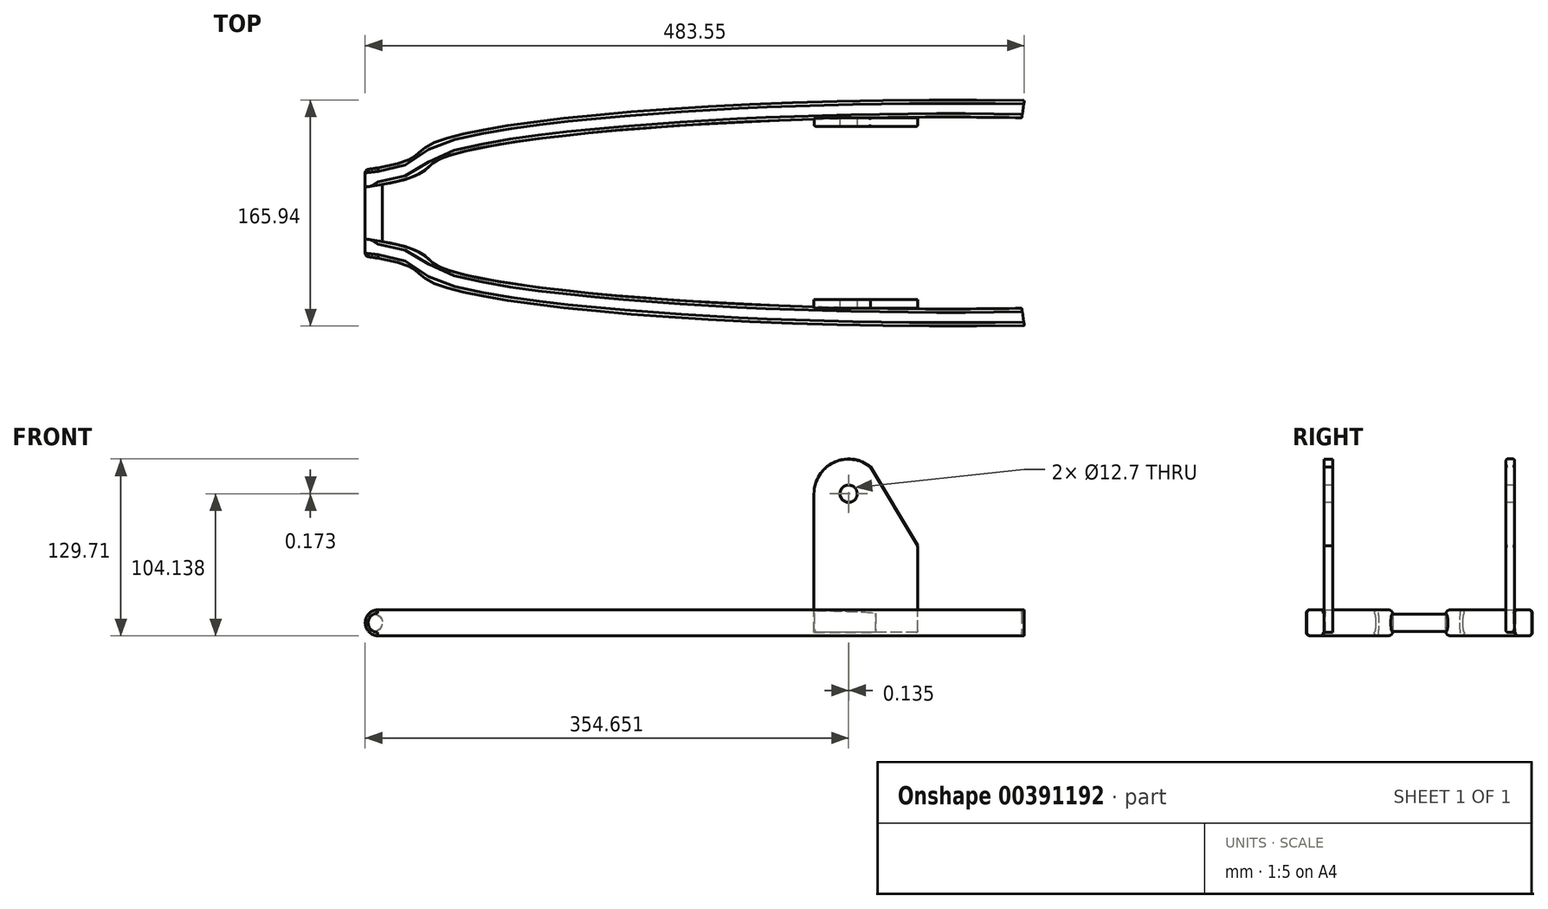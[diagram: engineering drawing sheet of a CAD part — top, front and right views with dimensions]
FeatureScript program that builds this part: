
annotation { "Feature Type Name" : "Feature", "Feature Type Description" : "" }
export const myFeature = defineFeature(function(context is Context, id is Id, definition is map)
    precondition{}
    {
        {
            var Q0;
            Q0=qCreatedBy(makeId("Front.planeOp"),FACE);
            var sketch = newSketch(context, id + "F0", { "sketchPlane" : qUnion([Q0])});
            skCircle(sketch, "E0", {"center": v(-33.3, 34.5) * mm, "radius": 6.35 * mm});
            skLineSegment(sketch, "E1", {"start": v(-33.3, 34.5) * mm, "end": v(-26.96, 34.5) * mm, "construction": true});
            skLineSegment(sketch, "E2", {"start": v(-33.3, 34.5) * mm, "end": v(-39.66, 34.5) * mm, "construction": true});
            skSolve(sketch);
        }
        {
            var Q0;
            Q0=makeQuery(id+"F0.imprint","IMPRINT",FACE,{"disambiguationData":[TD([[makeQuery(id+"F0.imprint","IMPRINT",EDGE,{"derivedFrom":sQuery(id+"F0.wireOp",EDGE,"E0")}),1.0]])]});
            var Q1;
            Q1 = qSketchRegion(id + "F0", true);
            extrude(context, id + "F1", {"entities" : qUnion([Q0, Q1]), "depth" : 50.8 * mm});
        }
        {
            var Q0;
            Q0=sQuery(id+"F0.wireOp",VERTEX,"E2.end");
            var Q1;
            Q1=qCreatedBy(makeId("Right.planeOp"),FACE);
            cPlane(context, id + "F2", {"entities" : qUnion([Q0, Q1]), "cplaneType" : CPlaneType.PLANE_POINT, "offset" : 25.4 * mm, "width" : 152.4 * mm, "height" : 152.4 * mm});
        }
        {
            var Q0;
            Q0=qCreatedBy(id+"F2.planeOp",FACE);
            var sketch = newSketch(context, id + "F3", { "sketchPlane" : qUnion([Q0])});
            skLineSegment(sketch, "E3.bottom", {"start": v(6.35, 44.02) * mm, "end": v(-6.35, 44.02) * mm});
            skLineSegment(sketch, "E3.top", {"start": v(6.35, 24.97) * mm, "end": v(-6.35, 24.97) * mm});
            skLineSegment(sketch, "E3.left", {"start": v(6.35, 44.02) * mm, "end": v(6.35, 24.97) * mm});
            skLineSegment(sketch, "E3.right", {"start": v(-6.35, 44.02) * mm, "end": v(-6.35, 24.97) * mm});
            skPoint(sketch, "E3.middle", {"position": v(0, 34.5) * mm});
            skLineSegment(sketch, "E4.bottom", {"start": v(-57.15, 44.02) * mm, "end": v(-44.45, 44.02) * mm});
            skLineSegment(sketch, "E4.top", {"start": v(-57.15, 24.97) * mm, "end": v(-44.45, 24.97) * mm});
            skLineSegment(sketch, "E4.left", {"start": v(-57.15, 44.02) * mm, "end": v(-57.15, 24.97) * mm});
            skLineSegment(sketch, "E4.right", {"start": v(-44.45, 44.02) * mm, "end": v(-44.45, 24.97) * mm});
            skPoint(sketch, "E4.middle", {"position": v(-50.8, 34.5) * mm});
            skSolve(sketch);
        }
        {
            var Q0;
            Q0=sQuery(id+"F3.wireOp",VERTEX,"E3.middle");
            var Q1;
            Q1=qCreatedBy(makeId("Top.planeOp"),FACE);
            cPlane(context, id + "F4", {"entities" : qUnion([Q0, Q1]), "cplaneType" : CPlaneType.PLANE_POINT, "offset" : 25.4 * mm, "width" : 152.4 * mm, "height" : 152.4 * mm});
        }
        {
            var Q0;
            Q0=qCreatedBy(id+"F4.planeOp",FACE);
            var sketch = newSketch(context, id + "F5", { "sketchPlane" : qUnion([Q0])});
            skFitSpline(sketch, "E5", {"points": [v(-39.66, 0) * mm, v(10.57, 19.05) * mm, v(442.94, 50.8) * mm], "startDerivative": vector(522.37, 69.74) * mm, "endDerivative": vector(821.5, -14.37) * mm});
            skLineSegment(sketch, "E6", {"start": v(-39.66, -25.4) * mm, "end": v(445.22, -25.4) * mm, "construction": true});
            skFitSpline(sketch, "E7.MirrorCS", {"points": [v(-39.66, -50.8) * mm, v(10.57, -69.85) * mm, v(442.94, -101.6) * mm], "startDerivative": vector(522.37, -69.74) * mm, "endDerivative": vector(821.5, 14.37) * mm});
            skLineSegment(sketch, "E8", {"start": v(-39.66, 77.86) * mm, "end": v(-39.66, -150.77) * mm, "construction": true});
            skSolve(sketch);
        }
        {
            var Q0;
            Q0=makeQuery(id+"F3.imprint","IMPRINT",FACE,{"disambiguationData":[TD([[makeQuery(id+"F3.imprint","IMPRINT",EDGE,{"derivedFrom":sQuery(id+"F3.wireOp",EDGE,"E3.bottom")}),1.0]])]});
            var Q1;
            Q1=sQuery(id+"F5.wireOp",EDGE,"E5");
            sweep(context, id + "F6", {"operationType" : NewBodyOperationType.ADD, "profiles" : qUnion([Q0]), "path" : qUnion([Q1])});
        }
        {
            var Q0;
            Q0=makeQuery(id+"F3.imprint","IMPRINT",FACE,{"disambiguationData":[TD([[makeQuery(id+"F3.imprint","IMPRINT",EDGE,{"derivedFrom":sQuery(id+"F3.wireOp",EDGE,"E4.bottom")}),-1.0]])]});
            var Q1;
            Q1=sQuery(id+"F5.wireOp",EDGE,"E7.MirrorCS");
            sweep(context, id + "F7", {"operationType" : NewBodyOperationType.ADD, "profiles" : qUnion([Q0]), "path" : qUnion([Q1])});
        }
        {
            var Q0;
            Q0=makeQuery(id+"F7.opSweep","CAP_EDGE",EDGE,{"disambiguationData":[OSD([sQuery(id+"F3.wireOp",EDGE,"E4.bottom"),sQuery(id+"F5.wireOp",VERTEX,"E7.MirrorCS.start")])],"isStart":true});
            var Q1;
            Q1=makeQuery(id+"F7.opSweep","CAP_EDGE",EDGE,{"disambiguationData":[OSD([sQuery(id+"F3.wireOp",EDGE,"E4.top"),sQuery(id+"F5.wireOp",VERTEX,"E7.MirrorCS.start")])],"isStart":true});
            fillet(context, id + "F8", {"entities" : qUnion([Q0, Q1]), "radius" : 9.52 * mm, "tangentPropagation" : true, "allowEdgeOverflow" : false});
        }
        {
            var Q0;
            Q0=makeQuery(id+"F6.opSweep","CAP_EDGE",EDGE,{"disambiguationData":[OSD([sQuery(id+"F3.wireOp",EDGE,"E3.top"),sQuery(id+"F5.wireOp",VERTEX,"E5.start")])],"isStart":true});
            var Q1;
            Q1=makeQuery(id+"F6.opSweep","CAP_EDGE",EDGE,{"disambiguationData":[OSD([sQuery(id+"F3.wireOp",EDGE,"E3.bottom"),sQuery(id+"F5.wireOp",VERTEX,"E5.start")])],"isStart":true});
            fillet(context, id + "F9", {"entities" : qUnion([Q0, Q1]), "radius" : 9.52 * mm, "tangentPropagation" : true, "allowEdgeOverflow" : false});
        }
        {
            var Q0;
            Q0=makeQuery(id+"F7.opSweep","SWEPT_EDGE",EDGE,{"disambiguationData":[OSD([sQuery(id+"F3.wireOp",EDGE,"E4.top"),sQuery(id+"F3.wireOp",EDGE,"E4.left"),sQuery(id+"F5.wireOp",EDGE,"E7.MirrorCS")])]});
            var Q1;
            Q1=makeQuery(id+"F7.opSweep","SWEPT_EDGE",EDGE,{"disambiguationData":[OSD([sQuery(id+"F3.wireOp",EDGE,"E4.bottom"),sQuery(id+"F3.wireOp",EDGE,"E4.left"),sQuery(id+"F5.wireOp",EDGE,"E7.MirrorCS")])]});
            var Q2;
            Q2=makeQuery(id+"F6.opSweep","SWEPT_EDGE",EDGE,{"disambiguationData":[OSD([sQuery(id+"F3.wireOp",EDGE,"E3.top"),sQuery(id+"F3.wireOp",EDGE,"E3.left"),sQuery(id+"F5.wireOp",EDGE,"E5")])]});
            var Q3;
            Q3=makeQuery(id+"F6.opSweep","SWEPT_EDGE",EDGE,{"disambiguationData":[OSD([sQuery(id+"F3.wireOp",EDGE,"E3.bottom"),sQuery(id+"F3.wireOp",EDGE,"E3.left"),sQuery(id+"F5.wireOp",EDGE,"E5")])]});
            fillet(context, id + "F10", {"entities" : qUnion([Q0, Q1, Q2, Q3]), "radius" : 2.54 * mm, "tangentPropagation" : true, "allowEdgeOverflow" : false});
        }
        {
            var Q0;
            Q0=makeQuery(id+"F6.opSweep","SWEPT_EDGE",EDGE,{"disambiguationData":[OSD([sQuery(id+"F3.wireOp",EDGE,"E3.top"),sQuery(id+"F3.wireOp",EDGE,"E3.right"),sQuery(id+"F5.wireOp",EDGE,"E5")])]});
            var Q1;
            Q1=makeQuery(id+"F6.opSweep","SWEPT_EDGE",EDGE,{"disambiguationData":[OSD([sQuery(id+"F3.wireOp",EDGE,"E3.bottom"),sQuery(id+"F3.wireOp",EDGE,"E3.right"),sQuery(id+"F5.wireOp",EDGE,"E5")])]});
            var Q2;
            Q2=makeQuery(id+"F7.opSweep","SWEPT_EDGE",EDGE,{"disambiguationData":[OSD([sQuery(id+"F3.wireOp",EDGE,"E4.top"),sQuery(id+"F3.wireOp",EDGE,"E4.right"),sQuery(id+"F5.wireOp",EDGE,"E7.MirrorCS")])]});
            var Q3;
            Q3=makeQuery(id+"F7.opSweep","SWEPT_EDGE",EDGE,{"disambiguationData":[OSD([sQuery(id+"F3.wireOp",EDGE,"E4.bottom"),sQuery(id+"F3.wireOp",EDGE,"E4.right"),sQuery(id+"F5.wireOp",EDGE,"E7.MirrorCS")])]});
            fillet(context, id + "F11", {"entities" : qUnion([Q0, Q1, Q2, Q3]), "radius" : 2.54 * mm, "allowEdgeOverflow" : false});
        }
        {
            var Q0;
            {var subQ0=sQuery(id+"F3.wireOp",EDGE,"E3.right");var subQ1=sQuery(id+"F3.wireOp",EDGE,"E3.bottom");var subQ2=sQuery(id+"F5.wireOp",EDGE,"E5");Q0=makeQuery(id+"F11.opFillet","BLEND_VERTEX",VERTEX,{"blendedFrom":[makeQuery(id+"F6.opSweep","SWEPT_EDGE",EDGE,{"disambiguationData":[OSD([subQ1,subQ0,subQ2])]}),makeQuery(id+"F6.opSweep","SWEPT_FACE",FACE,{"disambiguationData":[OSD([subQ0,subQ2])]}),makeQuery(id+"F6.opSweep","CAP_FACE",FACE,{"disambiguationData":[OSD([subQ1,sQuery(id+"F3.wireOp",EDGE,"E3.top"),sQuery(id+"F3.wireOp",EDGE,"E3.left"),subQ0,sQuery(id+"F5.wireOp",VERTEX,"E5.end")])],"isStart":false})],"blendedInto":[makeQuery(id+"F6.opSweep","SWEPT_FACE",FACE,{"disambiguationData":[OSD([subQ0,subQ2])]}),makeQuery(id+"F6.opSweep","CAP_FACE",FACE,{"disambiguationData":[OSD([subQ1,sQuery(id+"F3.wireOp",EDGE,"E3.top"),sQuery(id+"F3.wireOp",EDGE,"E3.left"),subQ0,sQuery(id+"F5.wireOp",VERTEX,"E5.end")])],"isStart":false})]});}
            var Q1;
            Q1=qCreatedBy(makeId("Front.planeOp"),FACE);
            cPlane(context, id + "F12", {"entities" : qUnion([Q0, Q1]), "cplaneType" : CPlaneType.PLANE_POINT, "offset" : 25.4 * mm, "width" : 152.4 * mm, "height" : 152.4 * mm});
        }
        {
            var Q0;
            Q0=qCreatedBy(id+"F12.planeOp",FACE);
            var sketch = newSketch(context, id + "F13", { "sketchPlane" : qUnion([Q0])});
            skLineSegment(sketch, "E9.bottom", {"start": v(365.8, 27.51) * mm, "end": v(289.73, 27.51) * mm});
            skLineSegment(sketch, "E9.left", {"start": v(365.8, 27.51) * mm, "end": v(365.8, 91.01) * mm});
            skLineSegment(sketch, "E9.right", {"start": v(289.73, 27.51) * mm, "end": v(289.73, 129.28) * mm});
            skLineSegment(sketch, "E10", {"start": v(330.87, 149.21) * mm, "end": v(365.8, 91.01) * mm});
            skCircle(sketch, "E11", {"center": v(315.13, 129.28) * mm, "radius": 6.35 * mm});
            skArc(sketch, "E12", {"start": v(330.87, 149.21) * mm, "mid": v(304.05, 152.14) * mm, "end": v(289.73, 129.28) * mm});
            skSolve(sketch);
        }
        {
            var Q0;
            Q0=makeQuery(id+"F13.imprint","IMPRINT",FACE,{"disambiguationData":[TD([[makeQuery(id+"F13.imprint","IMPRINT",EDGE,{"derivedFrom":sQuery(id+"F13.wireOp",EDGE,"E9.bottom")}),-1.0]])]});
            extrude(context, id + "F14", {"entities" : qUnion([Q0]), "operationType" : NewBodyOperationType.ADD, "depth" : 6.35 * mm});
        }
        {
            var Q0;
            Q0=makeQuery(id+"F14.opExtrude","CAP_EDGE",EDGE,{"disambiguationData":[OSD([sQuery(id+"F13.wireOp",EDGE,"E9.left")])],"isStart":true});
            var Q1;
            Q1=makeQuery(id+"F14.opExtrude","CAP_EDGE",EDGE,{"disambiguationData":[OSD([sQuery(id+"F13.wireOp",EDGE,"E9.left")])],"isStart":false});
            var Q2;
            Q2=makeQuery(id+"F14.opExtrude","SWEPT_EDGE",EDGE,{"disambiguationData":[OSD([sQuery(id+"F13.wireOp",EDGE,"E9.bottom"),sQuery(id+"F13.wireOp",EDGE,"E9.left")])]});
            var Q3;
            Q3=makeQuery(id+"F14.opExtrude","CAP_EDGE",EDGE,{"disambiguationData":[OSD([sQuery(id+"F13.wireOp",EDGE,"E9.bottom")])],"isStart":false});
            var Q4;
            Q4=makeQuery(id+"F14.opExtrude","CAP_EDGE",EDGE,{"disambiguationData":[OSD([sQuery(id+"F13.wireOp",EDGE,"E9.right")])],"isStart":true});
            var Q5;
            Q5=makeQuery(id+"F14.opExtrude","CAP_EDGE",EDGE,{"disambiguationData":[OSD([sQuery(id+"F13.wireOp",EDGE,"E9.right")])],"isStart":false});
            fillet(context, id + "F15", {"entities" : qUnion([Q0, Q1, Q2, Q3, Q4, Q5]), "radius" : 1.27 * mm, "tangentPropagation" : true, "allowEdgeOverflow" : false});
        }
        {
            var Q0;
            {var subQ0=sQuery(id+"F3.wireOp",EDGE,"E4.right");var subQ1=sQuery(id+"F3.wireOp",EDGE,"E4.bottom");var subQ2=sQuery(id+"F5.wireOp",EDGE,"E7.MirrorCS");Q0=makeQuery(id+"F11.opFillet","BLEND_VERTEX",VERTEX,{"blendedFrom":[makeQuery(id+"F7.opSweep","SWEPT_EDGE",EDGE,{"disambiguationData":[OSD([subQ1,subQ0,subQ2])]}),makeQuery(id+"F7.opSweep","SWEPT_FACE",FACE,{"disambiguationData":[OSD([subQ0,subQ2])]}),makeQuery(id+"F7.opSweep","CAP_FACE",FACE,{"disambiguationData":[OSD([subQ1,sQuery(id+"F3.wireOp",EDGE,"E4.top"),sQuery(id+"F3.wireOp",EDGE,"E4.left"),subQ0,sQuery(id+"F5.wireOp",VERTEX,"E7.MirrorCS.end")])],"isStart":false})],"blendedInto":[makeQuery(id+"F7.opSweep","SWEPT_FACE",FACE,{"disambiguationData":[OSD([subQ0,subQ2])]}),makeQuery(id+"F7.opSweep","CAP_FACE",FACE,{"disambiguationData":[OSD([subQ1,sQuery(id+"F3.wireOp",EDGE,"E4.top"),sQuery(id+"F3.wireOp",EDGE,"E4.left"),subQ0,sQuery(id+"F5.wireOp",VERTEX,"E7.MirrorCS.end")])],"isStart":false})]});}
            var Q1;
            Q1=qCreatedBy(makeId("Front.planeOp"),FACE);
            cPlane(context, id + "F16", {"entities" : qUnion([Q0, Q1]), "cplaneType" : CPlaneType.PLANE_POINT, "offset" : 25.4 * mm, "width" : 152.4 * mm, "height" : 152.4 * mm});
        }
        {
            var Q0;
            Q0=qCreatedBy(id+"F16.planeOp",FACE);
            var sketch = newSketch(context, id + "F17", { "sketchPlane" : qUnion([Q0])});
            skLineSegment(sketch, "E13.bottom", {"start": v(365.8, 27.5) * mm, "end": v(289.6, 27.5) * mm});
            skLineSegment(sketch, "E13.left", {"start": v(365.8, 27.5) * mm, "end": v(365.8, 91) * mm});
            skLineSegment(sketch, "E13.right", {"start": v(289.6, 27.5) * mm, "end": v(289.6, 129.1) * mm});
            skLineSegment(sketch, "E14", {"start": v(331.2, 148.67) * mm, "end": v(365.8, 91) * mm});
            skCircle(sketch, "E15", {"center": v(315, 129.1) * mm, "radius": 6.35 * mm});
            skArc(sketch, "E16", {"start": v(331.2, 148.67) * mm, "mid": v(304.18, 152.1) * mm, "end": v(289.6, 129.1) * mm});
            skSolve(sketch);
        }
        {
            var Q0;
            Q0=makeQuery(id+"F17.imprint","IMPRINT",FACE,{"disambiguationData":[TD([[makeQuery(id+"F17.imprint","IMPRINT",EDGE,{"derivedFrom":sQuery(id+"F17.wireOp",EDGE,"E13.bottom")}),-1.0]])]});
            extrude(context, id + "F18", {"entities" : qUnion([Q0]), "operationType" : NewBodyOperationType.ADD, "oppositeDirection" : true, "depth" : 6.35 * mm});
        }
        {
            var Q0;
            Q0=makeQuery(id+"F14.opExtrude","CAP_EDGE",EDGE,{"disambiguationData":[OSD([sQuery(id+"F13.wireOp",EDGE,"E10")])],"isStart":false});
            fillet(context, id + "F19", {"entities" : qUnion([Q0]), "radius" : 1.27 * mm, "tangentPropagation" : true, "allowEdgeOverflow" : false});
        }
    });
